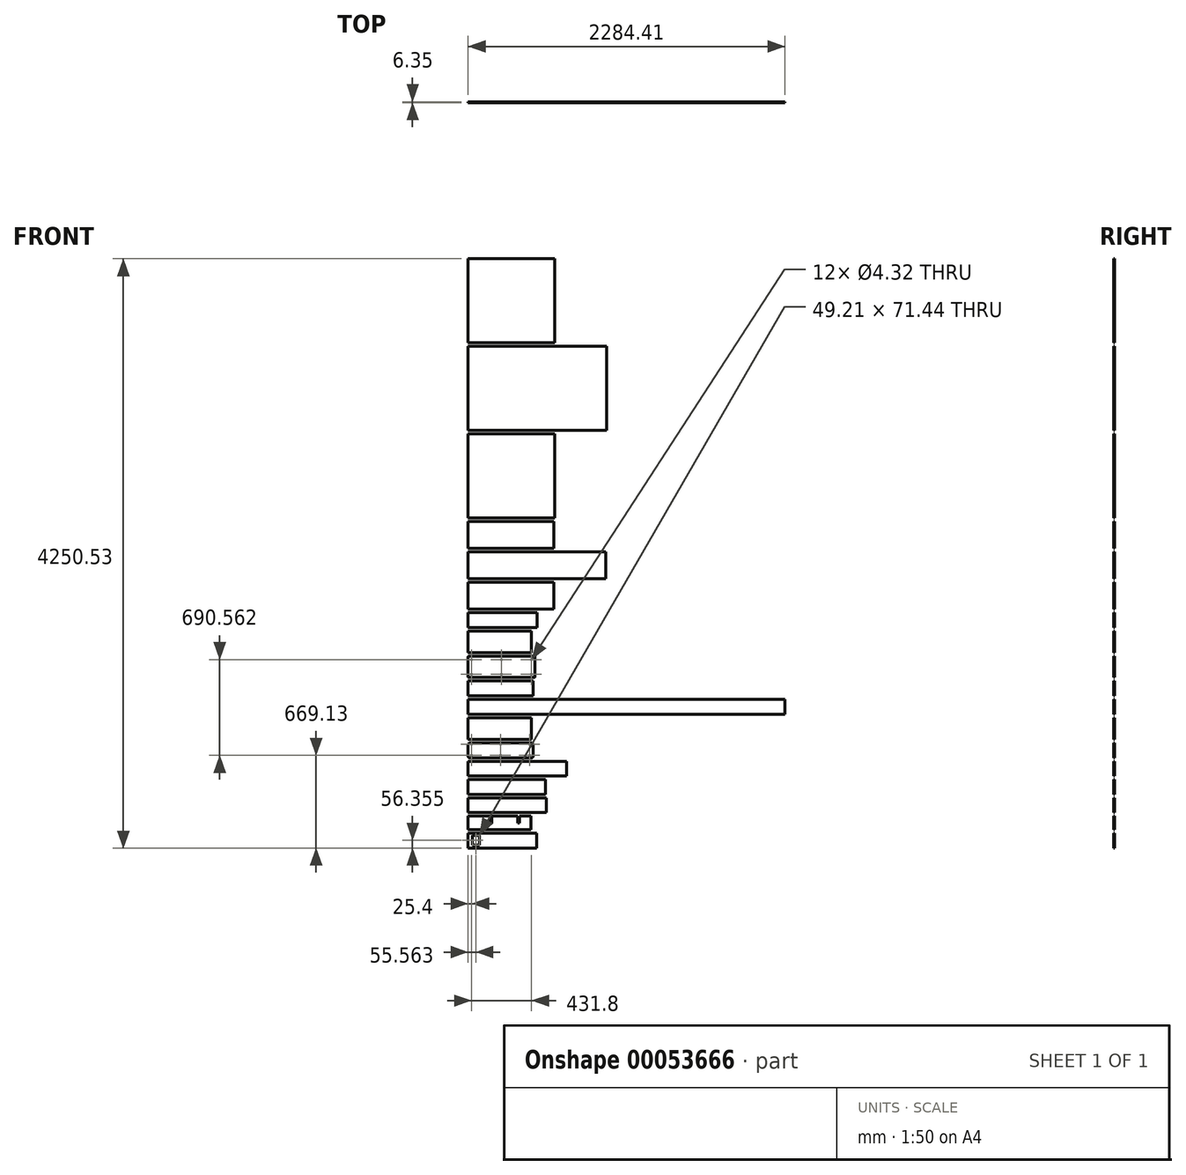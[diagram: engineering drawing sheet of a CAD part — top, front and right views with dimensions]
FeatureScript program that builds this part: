
annotation { "Feature Type Name" : "Feature", "Feature Type Description" : "" }
export const myFeature = defineFeature(function(context is Context, id is Id, definition is map)
    precondition{}
    {
        {
            var Q0;
            Q0=qCreatedBy(makeId("Front.planeOp"),FACE);
            var sketch = newSketch(context, id + "F0", { "sketchPlane" : qUnion([Q0])});
            skLineSegment(sketch, "E0", {"start": v(0, 0) * mm, "end": v(0, -25400) * mm, "construction": true});
            skLineSegment(sketch, "E1.bottom", {"start": v(0, -25.4) * mm, "end": v(623.89, -25.4) * mm});
            skLineSegment(sketch, "E1.top", {"start": v(0, -631.83) * mm, "end": v(623.89, -631.83) * mm});
            skLineSegment(sketch, "E1.left", {"start": v(0, -25.4) * mm, "end": v(0, -631.83) * mm});
            skLineSegment(sketch, "E1.right", {"start": v(623.89, -25.4) * mm, "end": v(623.89, -631.83) * mm});
            skLineSegment(sketch, "E2.bottom", {"start": v(0, -657.23) * mm, "end": v(998.54, -657.23) * mm});
            skLineSegment(sketch, "E2.top", {"start": v(0, -1263.65) * mm, "end": v(998.54, -1263.65) * mm});
            skLineSegment(sketch, "E2.left", {"start": v(0, -657.23) * mm, "end": v(0, -1263.65) * mm});
            skLineSegment(sketch, "E2.right", {"start": v(998.54, -657.23) * mm, "end": v(998.54, -1263.65) * mm});
            skLineSegment(sketch, "E3.bottom", {"start": v(0, -1289.05) * mm, "end": v(623.89, -1289.05) * mm});
            skLineSegment(sketch, "E3.top", {"start": v(0, -1895.48) * mm, "end": v(623.89, -1895.48) * mm});
            skLineSegment(sketch, "E3.left", {"start": v(0, -1289.05) * mm, "end": v(0, -1895.48) * mm});
            skLineSegment(sketch, "E3.right", {"start": v(623.89, -1289.05) * mm, "end": v(623.89, -1895.48) * mm});
            skLineSegment(sketch, "E4.bottom", {"start": v(0, -1920.88) * mm, "end": v(619.13, -1920.88) * mm});
            skLineSegment(sketch, "E4.top", {"start": v(0, -2114.55) * mm, "end": v(619.13, -2114.55) * mm});
            skLineSegment(sketch, "E4.left", {"start": v(0, -1920.88) * mm, "end": v(0, -2114.55) * mm});
            skLineSegment(sketch, "E4.right", {"start": v(619.13, -1920.88) * mm, "end": v(619.13, -2114.55) * mm});
            skLineSegment(sketch, "E5.bottom", {"start": v(0, -2139.95) * mm, "end": v(992.19, -2139.95) * mm});
            skLineSegment(sketch, "E5.top", {"start": v(0, -2333.62) * mm, "end": v(992.19, -2333.62) * mm});
            skLineSegment(sketch, "E5.left", {"start": v(0, -2139.95) * mm, "end": v(0, -2333.62) * mm});
            skLineSegment(sketch, "E5.right", {"start": v(992.19, -2139.95) * mm, "end": v(992.19, -2333.62) * mm});
            skLineSegment(sketch, "E6.bottom", {"start": v(0, -2359.03) * mm, "end": v(619.13, -2359.03) * mm});
            skLineSegment(sketch, "E6.top", {"start": v(0, -2552.7) * mm, "end": v(619.13, -2552.7) * mm});
            skLineSegment(sketch, "E6.left", {"start": v(0, -2359.03) * mm, "end": v(0, -2552.7) * mm});
            skLineSegment(sketch, "E6.right", {"start": v(619.13, -2359.03) * mm, "end": v(619.13, -2552.7) * mm});
            skLineSegment(sketch, "E7.bottom", {"start": v(0, -2578.1) * mm, "end": v(497.68, -2578.1) * mm});
            skLineSegment(sketch, "E7.top", {"start": v(0, -2686.05) * mm, "end": v(497.68, -2686.05) * mm});
            skLineSegment(sketch, "E7.left", {"start": v(0, -2578.1) * mm, "end": v(0, -2686.05) * mm});
            skLineSegment(sketch, "E7.right", {"start": v(497.68, -2578.1) * mm, "end": v(497.68, -2686.05) * mm});
            skLineSegment(sketch, "E8.bottom", {"start": v(0, -2711.45) * mm, "end": v(457.2, -2711.45) * mm});
            skLineSegment(sketch, "E8.top", {"start": v(0, -2867.03) * mm, "end": v(457.2, -2867.03) * mm});
            skLineSegment(sketch, "E8.left", {"start": v(0, -2711.45) * mm, "end": v(0, -2867.03) * mm});
            skLineSegment(sketch, "E8.right", {"start": v(457.2, -2711.45) * mm, "end": v(457.2, -2867.03) * mm});
            skLineSegment(sketch, "E9.bottom", {"start": v(3.18, -2892.42) * mm, "end": v(479.43, -2892.42) * mm});
            skLineSegment(sketch, "E9.top", {"start": v(3.18, -3044.82) * mm, "end": v(479.43, -3044.82) * mm});
            skLineSegment(sketch, "E9.left", {"start": v(0, -2895.6) * mm, "end": v(0, -3041.65) * mm});
            skLineSegment(sketch, "E9.right", {"start": v(482.6, -2895.6) * mm, "end": v(482.6, -3041.65) * mm});
            skPoint(sketch, "E10.visualSharp", {"position": v(0, -2892.42) * mm});
            skArc(sketch, "E10.filletArc", {"start": v(3.18, -2892.42) * mm, "mid": v(0.93, -2893.35) * mm, "end": v(0, -2895.6) * mm});
            skPoint(sketch, "E11.visualSharp", {"position": v(482.6, -2892.42) * mm});
            skArc(sketch, "E11.filletArc", {"start": v(482.6, -2895.6) * mm, "mid": v(481.67, -2893.35) * mm, "end": v(479.43, -2892.42) * mm});
            skPoint(sketch, "E12.visualSharp", {"position": v(482.6, -3044.82) * mm});
            skArc(sketch, "E12.filletArc", {"start": v(479.43, -3044.82) * mm, "mid": v(481.67, -3043.9) * mm, "end": v(482.6, -3041.65) * mm});
            skPoint(sketch, "E13.visualSharp", {"position": v(0, -3044.82) * mm});
            skArc(sketch, "E13.filletArc", {"start": v(0, -3041.65) * mm, "mid": v(0.93, -3043.9) * mm, "end": v(3.18, -3044.82) * mm});
            skLineSegment(sketch, "E14.bottom", {"start": v(0, -3070.22) * mm, "end": v(468.31, -3070.22) * mm});
            skLineSegment(sketch, "E14.top", {"start": v(0, -3178.18) * mm, "end": v(468.31, -3178.18) * mm});
            skLineSegment(sketch, "E14.left", {"start": v(0, -3070.22) * mm, "end": v(0, -3178.18) * mm});
            skLineSegment(sketch, "E14.right", {"start": v(468.31, -3070.22) * mm, "end": v(468.31, -3178.18) * mm});
            skLineSegment(sketch, "E15.bottom", {"start": v(0, -3203.57) * mm, "end": v(2284.41, -3203.57) * mm});
            skLineSegment(sketch, "E15.top", {"start": v(0, -3311.53) * mm, "end": v(2284.41, -3311.53) * mm});
            skLineSegment(sketch, "E15.left", {"start": v(0, -3203.57) * mm, "end": v(0, -3311.53) * mm});
            skLineSegment(sketch, "E15.right", {"start": v(2284.41, -3203.57) * mm, "end": v(2284.41, -3311.53) * mm});
            skLineSegment(sketch, "E16", {"start": v(1303.34, -3203.57) * mm, "end": v(1411.29, -3311.53) * mm, "construction": true});
            skLineSegment(sketch, "E17.bottom", {"start": v(0, -3336.92) * mm, "end": v(455.61, -3336.92) * mm});
            skLineSegment(sketch, "E17.top", {"start": v(0, -3492.5) * mm, "end": v(455.61, -3492.5) * mm});
            skLineSegment(sketch, "E17.left", {"start": v(0, -3336.92) * mm, "end": v(0, -3492.5) * mm});
            skLineSegment(sketch, "E17.right", {"start": v(455.61, -3336.92) * mm, "end": v(455.61, -3492.5) * mm});
            skLineSegment(sketch, "E18.bottom", {"start": v(12.7, -3517.9) * mm, "end": v(455.61, -3517.9) * mm});
            skLineSegment(sketch, "E18.top", {"start": v(12.7, -3625.85) * mm, "end": v(455.61, -3625.85) * mm});
            skLineSegment(sketch, "E18.left", {"start": v(0, -3530.6) * mm, "end": v(0, -3613.15) * mm});
            skLineSegment(sketch, "E18.right", {"start": v(468.31, -3530.6) * mm, "end": v(468.31, -3613.15) * mm});
            skPoint(sketch, "E19.visualSharp", {"position": v(468.31, -3517.9) * mm});
            skArc(sketch, "E19.filletArc", {"start": v(468.31, -3530.6) * mm, "mid": v(464.6, -3521.62) * mm, "end": v(455.61, -3517.9) * mm});
            skPoint(sketch, "E20.visualSharp", {"position": v(468.31, -3625.85) * mm});
            skArc(sketch, "E20.filletArc", {"start": v(455.61, -3625.85) * mm, "mid": v(464.6, -3622.13) * mm, "end": v(468.31, -3613.15) * mm});
            skPoint(sketch, "E21.visualSharp", {"position": v(0, -3625.85) * mm});
            skArc(sketch, "E21.filletArc", {"start": v(0, -3613.15) * mm, "mid": v(3.72, -3622.13) * mm, "end": v(12.7, -3625.85) * mm});
            skPoint(sketch, "E22.visualSharp", {"position": v(0, -3517.9) * mm});
            skArc(sketch, "E22.filletArc", {"start": v(12.7, -3517.9) * mm, "mid": v(3.72, -3521.62) * mm, "end": v(0, -3530.6) * mm});
            skLineSegment(sketch, "E23.bottom", {"start": v(0, -3651.25) * mm, "end": v(709.61, -3651.25) * mm});
            skLineSegment(sketch, "E23.top", {"start": v(0, -3756.82) * mm, "end": v(709.61, -3756.82) * mm});
            skLineSegment(sketch, "E23.left", {"start": v(0, -3651.25) * mm, "end": v(0, -3756.82) * mm});
            skLineSegment(sketch, "E23.right", {"start": v(709.61, -3651.25) * mm, "end": v(709.61, -3756.82) * mm});
            skLineSegment(sketch, "E24.bottom", {"start": v(0, -3782.22) * mm, "end": v(557.21, -3782.22) * mm});
            skLineSegment(sketch, "E24.top", {"start": v(0, -3887.79) * mm, "end": v(557.21, -3887.79) * mm});
            skLineSegment(sketch, "E24.left", {"start": v(0, -3782.22) * mm, "end": v(0, -3887.79) * mm});
            skLineSegment(sketch, "E24.right", {"start": v(557.21, -3782.22) * mm, "end": v(557.21, -3887.79) * mm});
            skLineSegment(sketch, "E25.bottom", {"start": v(0, -3913.19) * mm, "end": v(565.15, -3913.19) * mm});
            skLineSegment(sketch, "E25.top", {"start": v(0, -4018.76) * mm, "end": v(565.15, -4018.76) * mm});
            skLineSegment(sketch, "E25.left", {"start": v(0, -3913.19) * mm, "end": v(0, -4018.76) * mm});
            skLineSegment(sketch, "E25.right", {"start": v(565.15, -3913.19) * mm, "end": v(565.15, -4018.76) * mm});
            skLineSegment(sketch, "E26.bottom", {"start": v(0, -4044.16) * mm, "end": v(160.34, -4044.16) * mm});
            skLineSegment(sketch, "E26.top", {"start": v(0, -4142.58) * mm, "end": v(454.03, -4142.58) * mm});
            skLineSegment(sketch, "E26.left", {"start": v(0, -4044.16) * mm, "end": v(0, -4142.58) * mm});
            skLineSegment(sketch, "E26.right", {"start": v(454.03, -4044.16) * mm, "end": v(454.03, -4142.58) * mm});
            skLineSegment(sketch, "E27.top", {"start": v(160.34, -4094.96) * mm, "end": v(171.45, -4094.96) * mm});
            skLineSegment(sketch, "E27.left", {"start": v(160.34, -4044.16) * mm, "end": v(160.34, -4094.96) * mm});
            skLineSegment(sketch, "E27.right", {"start": v(171.45, -4044.16) * mm, "end": v(171.45, -4094.96) * mm});
            skLineSegment(sketch, "E28.top", {"start": v(357.98, -4094.96) * mm, "end": v(369.1, -4094.96) * mm});
            skLineSegment(sketch, "E28.left", {"start": v(357.98, -4044.16) * mm, "end": v(357.98, -4094.96) * mm});
            skLineSegment(sketch, "E28.right", {"start": v(369.1, -4044.16) * mm, "end": v(369.1, -4094.96) * mm});
            skLineSegment(sketch, "E29.trimOffspring", {"start": v(171.45, -4044.16) * mm, "end": v(357.98, -4044.16) * mm});
            skLineSegment(sketch, "E30.trimOffspring", {"start": v(369.1, -4044.16) * mm, "end": v(454.03, -4044.16) * mm});
            skLineSegment(sketch, "E31.bottom", {"start": v(0, -4167.98) * mm, "end": v(493.71, -4167.98) * mm});
            skLineSegment(sketch, "E31.top", {"start": v(0, -4275.93) * mm, "end": v(493.71, -4275.93) * mm});
            skLineSegment(sketch, "E31.left", {"start": v(0, -4167.98) * mm, "end": v(0, -4275.93) * mm});
            skLineSegment(sketch, "E31.right", {"start": v(493.71, -4167.98) * mm, "end": v(493.71, -4275.93) * mm});
            skLineSegment(sketch, "E32.bottom", {"start": v(30.96, -4183.86) * mm, "end": v(80.17, -4183.86) * mm});
            skLineSegment(sketch, "E32.top", {"start": v(30.96, -4255.3) * mm, "end": v(80.17, -4255.3) * mm});
            skLineSegment(sketch, "E32.left", {"start": v(30.96, -4183.86) * mm, "end": v(30.96, -4255.3) * mm});
            skLineSegment(sketch, "E32.right", {"start": v(80.17, -4183.86) * mm, "end": v(80.17, -4255.3) * mm});
            skLineSegment(sketch, "E33.bottom", {"start": v(25.4, -2916.24) * mm, "end": v(457.2, -2916.24) * mm, "construction": true});
            skLineSegment(sketch, "E33.top", {"start": v(25.4, -3021.01) * mm, "end": v(457.2, -3021.01) * mm, "construction": true});
            skLineSegment(sketch, "E33.left", {"start": v(25.4, -2916.24) * mm, "end": v(25.4, -3021.01) * mm, "construction": true});
            skLineSegment(sketch, "E33.right", {"start": v(457.2, -2916.24) * mm, "end": v(457.2, -3021.01) * mm, "construction": true});
            skCircle(sketch, "E34", {"center": v(25.4, -2916.24) * mm, "radius": 2.16 * mm});
            skCircle(sketch, "E35", {"center": v(25.4, -3021.01) * mm, "radius": 2.16 * mm});
            skCircle(sketch, "E36", {"center": v(457.2, -3021.01) * mm, "radius": 2.16 * mm});
            skCircle(sketch, "E37", {"center": v(457.2, -2916.24) * mm, "radius": 2.16 * mm});
            skCircle(sketch, "E38", {"center": v(241.3, -3021.01) * mm, "radius": 2.16 * mm});
            skCircle(sketch, "E39", {"center": v(241.3, -2916.24) * mm, "radius": 2.16 * mm});
            skLineSegment(sketch, "E40.bottom", {"start": v(25.4, -3527.42) * mm, "end": v(442.91, -3527.42) * mm, "construction": true});
            skLineSegment(sketch, "E40.top", {"start": v(25.4, -3606.8) * mm, "end": v(442.91, -3606.8) * mm, "construction": true});
            skLineSegment(sketch, "E40.left", {"start": v(25.4, -3527.42) * mm, "end": v(25.4, -3606.8) * mm, "construction": true});
            skLineSegment(sketch, "E40.right", {"start": v(442.91, -3527.42) * mm, "end": v(442.91, -3606.8) * mm, "construction": true});
            skCircle(sketch, "E41", {"center": v(25.4, -3527.42) * mm, "radius": 2.16 * mm});
            skCircle(sketch, "E42", {"center": v(25.4, -3606.8) * mm, "radius": 2.16 * mm});
            skCircle(sketch, "E43", {"center": v(234.16, -3527.42) * mm, "radius": 2.16 * mm});
            skCircle(sketch, "E44", {"center": v(234.16, -3606.8) * mm, "radius": 2.16 * mm});
            skCircle(sketch, "E45", {"center": v(442.91, -3606.8) * mm, "radius": 2.16 * mm});
            skCircle(sketch, "E46", {"center": v(442.91, -3527.42) * mm, "radius": 2.16 * mm});
            skSolve(sketch);
        }
        {
            var Q0;
            Q0 = qSketchRegion(id + "F0", true);
            extrude(context, id + "F1", {"entities" : qUnion([Q0]), "depth" : 6.35 * mm});
        }
    });
